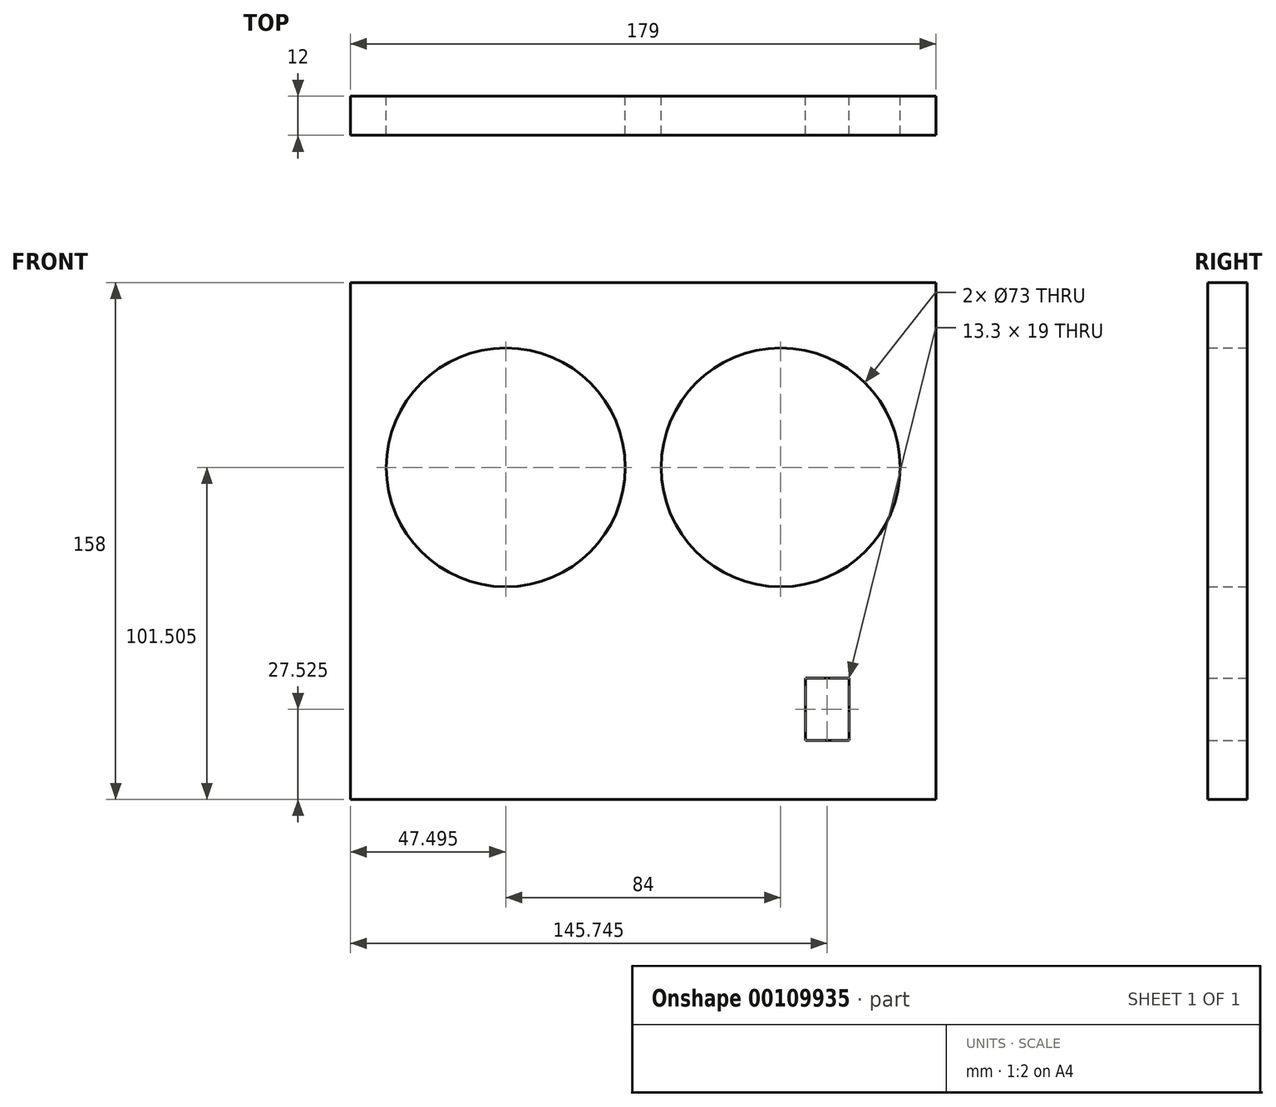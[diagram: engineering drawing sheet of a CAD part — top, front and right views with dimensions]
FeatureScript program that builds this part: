
annotation { "Feature Type Name" : "Feature", "Feature Type Description" : "" }
export const myFeature = defineFeature(function(context is Context, id is Id, definition is map)
    precondition{}
    {
        {
            var Q0;
            Q0=qCreatedBy(makeId("Front.planeOp"),FACE);
            var sketch = newSketch(context, id + "F0", { "sketchPlane" : qUnion([Q0])});
            skLineSegment(sketch, "E0", {"start": v(-38.24, 136.73) * mm, "end": v(-38.24, -21.27) * mm});
            skLineSegment(sketch, "E1", {"start": v(-38.24, -21.27) * mm, "end": v(140.76, -21.27) * mm});
            skLineSegment(sketch, "E2", {"start": v(140.76, -21.27) * mm, "end": v(140.76, 136.73) * mm});
            skLineSegment(sketch, "E3", {"start": v(140.76, 136.73) * mm, "end": v(-38.24, 136.73) * mm});
            skCircle(sketch, "E4", {"center": v(9.26, 80.23) * mm, "radius": 36.5 * mm});
            skCircle(sketch, "E5", {"center": v(93.26, 80.23) * mm, "radius": 36.5 * mm});
            skLineSegment(sketch, "E6", {"start": v(100.86, -3.25) * mm, "end": v(114.16, -3.25) * mm});
            skLineSegment(sketch, "E7", {"start": v(114.16, -3.25) * mm, "end": v(114.16, 15.75) * mm});
            skLineSegment(sketch, "E8", {"start": v(114.16, 15.75) * mm, "end": v(100.86, 15.75) * mm});
            skLineSegment(sketch, "E9", {"start": v(100.86, 15.75) * mm, "end": v(100.86, -3.25) * mm});
            skSolve(sketch);
        }
        {
            var Q0;
            Q0=makeQuery(id+"F0.imprint","IMPRINT",FACE,{"disambiguationData":[TD([[makeQuery(id+"F0.imprint","IMPRINT",EDGE,{"derivedFrom":sQuery(id+"F0.wireOp",EDGE,"E0")}),1.0]])]});
            extrude(context, id + "F1", {"entities" : qUnion([Q0]), "depth" : 12 * mm});
        }
    });
